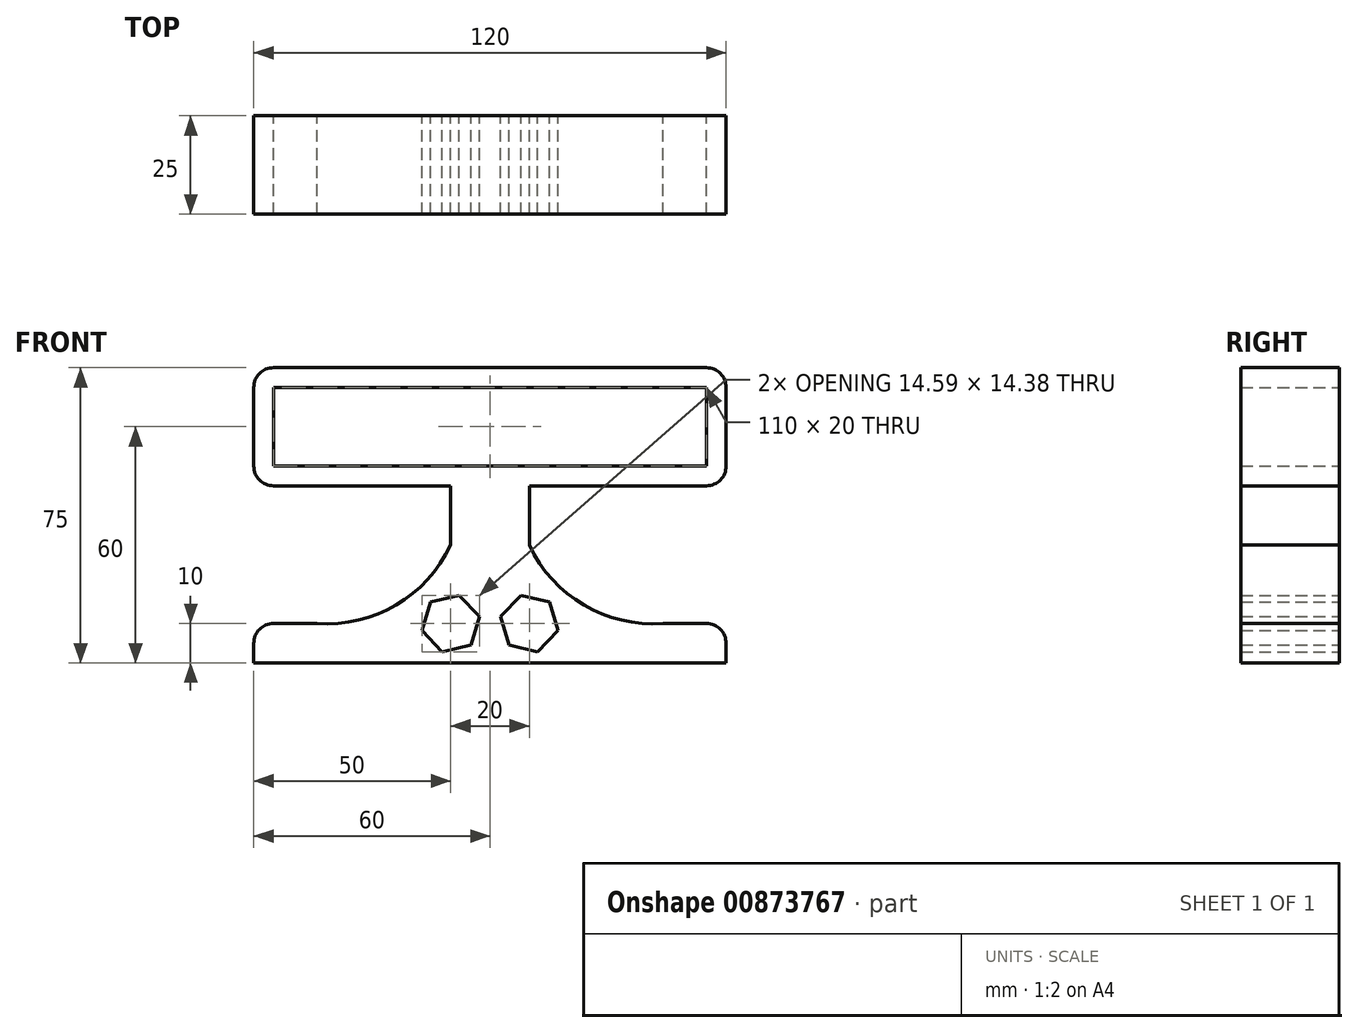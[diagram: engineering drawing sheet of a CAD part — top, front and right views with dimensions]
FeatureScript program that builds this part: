
annotation { "Feature Type Name" : "Feature", "Feature Type Description" : "" }
export const myFeature = defineFeature(function(context is Context, id is Id, definition is map)
    precondition{}
    {
        {
            var Q0;
            Q0=qCreatedBy(makeId("Front.planeOp"),FACE);
            var sketch = newSketch(context, id + "F0", { "sketchPlane" : qUnion([Q0])});
            skLineSegment(sketch, "E0", {"start": v(0, 0) * mm, "end": v(60, 0) * mm});
            skLineSegment(sketch, "E1", {"start": v(60, 0) * mm, "end": v(60, 5) * mm});
            skLineSegment(sketch, "E2", {"start": v(55, 10) * mm, "end": v(43.9, 10) * mm});
            skLineSegment(sketch, "E3", {"start": v(10, 29.9) * mm, "end": v(10, 45) * mm});
            skLineSegment(sketch, "E4", {"start": v(10, 45) * mm, "end": v(55, 45) * mm});
            skLineSegment(sketch, "E5", {"start": v(60, 50) * mm, "end": v(60, 70) * mm});
            skLineSegment(sketch, "E6", {"start": v(0, 0) * mm, "end": v(0, -36.27) * mm, "construction": true});
            skLineSegment(sketch, "E7", {"start": v(55, 75) * mm, "end": v(0, 75) * mm});
            skLineSegment(sketch, "E8", {"start": v(0, 70) * mm, "end": v(55, 70) * mm});
            skLineSegment(sketch, "E9", {"start": v(55, 70) * mm, "end": v(55, 50) * mm});
            skLineSegment(sketch, "E10", {"start": v(55, 50) * mm, "end": v(0, 50) * mm});
            skPoint(sketch, "E11.visualSharp", {"position": v(60, 45) * mm});
            skArc(sketch, "E11.filletArc", {"start": v(55, 45) * mm, "mid": v(58.54, 46.46) * mm, "end": v(60, 50) * mm});
            skPoint(sketch, "E12.visualSharp", {"position": v(60, 75) * mm});
            skArc(sketch, "E12.filletArc", {"start": v(60, 70) * mm, "mid": v(58.54, 73.54) * mm, "end": v(55, 75) * mm});
            skPoint(sketch, "E13.MirrorCS.start.orphan", {"position": v(0, 0) * mm});
            skPoint(sketch, "E14.MirrorCS.end.orphan", {"position": v(0, 50) * mm});
            skPoint(sketch, "E15.MirrorCS.start.orphan", {"position": v(0, 70) * mm});
            skPoint(sketch, "E16.MirrorCS.end.orphan", {"position": v(0, 75) * mm});
            skPoint(sketch, "E17.visualSharp", {"position": v(60, 10) * mm});
            skArc(sketch, "E17.filletArc", {"start": v(60, 5) * mm, "mid": v(58.54, 8.54) * mm, "end": v(55, 10) * mm});
            skArc(sketch, "E18", {"start": v(10, 29.9) * mm, "mid": v(23.87, 14.7) * mm, "end": v(43.9, 10) * mm});
            skCircle(sketch, "E19.cCircle", {"center": v(10, 10) * mm, "radius": 7.5 * mm, "construction": true});
            skLineSegment(sketch, "E19.0", {"start": v(17.3, 8.26) * mm, "end": v(12.14, 2.81) * mm});
            skLineSegment(sketch, "E19.1", {"start": v(12.14, 2.81) * mm, "end": v(4.84, 4.56) * mm});
            skLineSegment(sketch, "E19.2", {"start": v(4.84, 4.56) * mm, "end": v(2.7, 11.74) * mm});
            skLineSegment(sketch, "E19.3", {"start": v(2.7, 11.74) * mm, "end": v(7.86, 17.19) * mm});
            skLineSegment(sketch, "E19.4", {"start": v(7.86, 17.19) * mm, "end": v(15.16, 15.44) * mm});
            skLineSegment(sketch, "E19.5", {"start": v(15.16, 15.44) * mm, "end": v(17.3, 8.26) * mm});
            skArc(sketch, "E20.MirrorCS", {"start": v(-55, 45) * mm, "mid": v(-58.54, 46.46) * mm, "end": v(-60, 50) * mm});
            skArc(sketch, "E21.MirrorCS", {"start": v(-60, 70) * mm, "mid": v(-58.54, 73.54) * mm, "end": v(-55, 75) * mm});
            skArc(sketch, "E22.MirrorCS", {"start": v(-60, 5) * mm, "mid": v(-58.54, 8.54) * mm, "end": v(-55, 10) * mm});
            skLineSegment(sketch, "E23.MirrorCS", {"start": v(-17.3, 8.26) * mm, "end": v(-12.14, 2.81) * mm});
            skLineSegment(sketch, "E24.MirrorCS", {"start": v(-60, 50) * mm, "end": v(-60, 70) * mm});
            skPoint(sketch, "E25.MirrorP", {"position": v(-60, 45) * mm});
            skPoint(sketch, "E26.MirrorP", {"position": v(-60, 10) * mm});
            skLineSegment(sketch, "E27.MirrorCS", {"start": v(-55, 75) * mm, "end": v(0, 75) * mm});
            skLineSegment(sketch, "E28.MirrorCS", {"start": v(-7.86, 17.19) * mm, "end": v(-15.16, 15.44) * mm});
            skCircle(sketch, "E29.MirrorC", {"center": v(-10, 10) * mm, "radius": 7.5 * mm, "construction": true});
            skLineSegment(sketch, "E30.MirrorCS", {"start": v(-10, 45) * mm, "end": v(-55, 45) * mm});
            skArc(sketch, "E31.MirrorCS", {"start": v(-10, 29.9) * mm, "mid": v(-23.87, 14.7) * mm, "end": v(-43.9, 10) * mm});
            skLineSegment(sketch, "E32.MirrorCS", {"start": v(-60, 0) * mm, "end": v(-60, 5) * mm});
            skLineSegment(sketch, "E33.MirrorCS", {"start": v(-55, 70) * mm, "end": v(-55, 50) * mm});
            skLineSegment(sketch, "E34.MirrorCS", {"start": v(-2.7, 11.74) * mm, "end": v(-7.86, 17.19) * mm});
            skLineSegment(sketch, "E35.MirrorCS", {"start": v(-55, 50) * mm, "end": v(0, 50) * mm});
            skLineSegment(sketch, "E36.MirrorCS", {"start": v(-55, 10) * mm, "end": v(-43.9, 10) * mm});
            skLineSegment(sketch, "E37.MirrorCS", {"start": v(0, 70) * mm, "end": v(-55, 70) * mm});
            skPoint(sketch, "E38.MirrorP", {"position": v(-60, 75) * mm});
            skLineSegment(sketch, "E39.MirrorCS", {"start": v(-12.14, 2.81) * mm, "end": v(-4.84, 4.56) * mm});
            skLineSegment(sketch, "E40.MirrorCS", {"start": v(-10, 29.9) * mm, "end": v(-10, 45) * mm});
            skLineSegment(sketch, "E41.MirrorCS", {"start": v(0, 0) * mm, "end": v(-60, 0) * mm});
            skLineSegment(sketch, "E42.MirrorCS", {"start": v(-4.84, 4.56) * mm, "end": v(-2.7, 11.74) * mm});
            skLineSegment(sketch, "E43.MirrorCS", {"start": v(-15.16, 15.44) * mm, "end": v(-17.3, 8.26) * mm});
            skSolve(sketch);
        }
        {
            var Q0;
            Q0=makeQuery(id+"F0.imprint","IMPRINT",FACE,{"disambiguationData":[TD([[makeQuery(id+"F0.imprint","IMPRINT",EDGE,{"derivedFrom":sQuery(id+"F0.wireOp",EDGE,"E0")}),1.0]])]});
            extrude(context, id + "F1", {"entities" : qUnion([Q0]), "depth" : 25 * mm, "offsetDistance" : 25 * mm});
        }
    });
